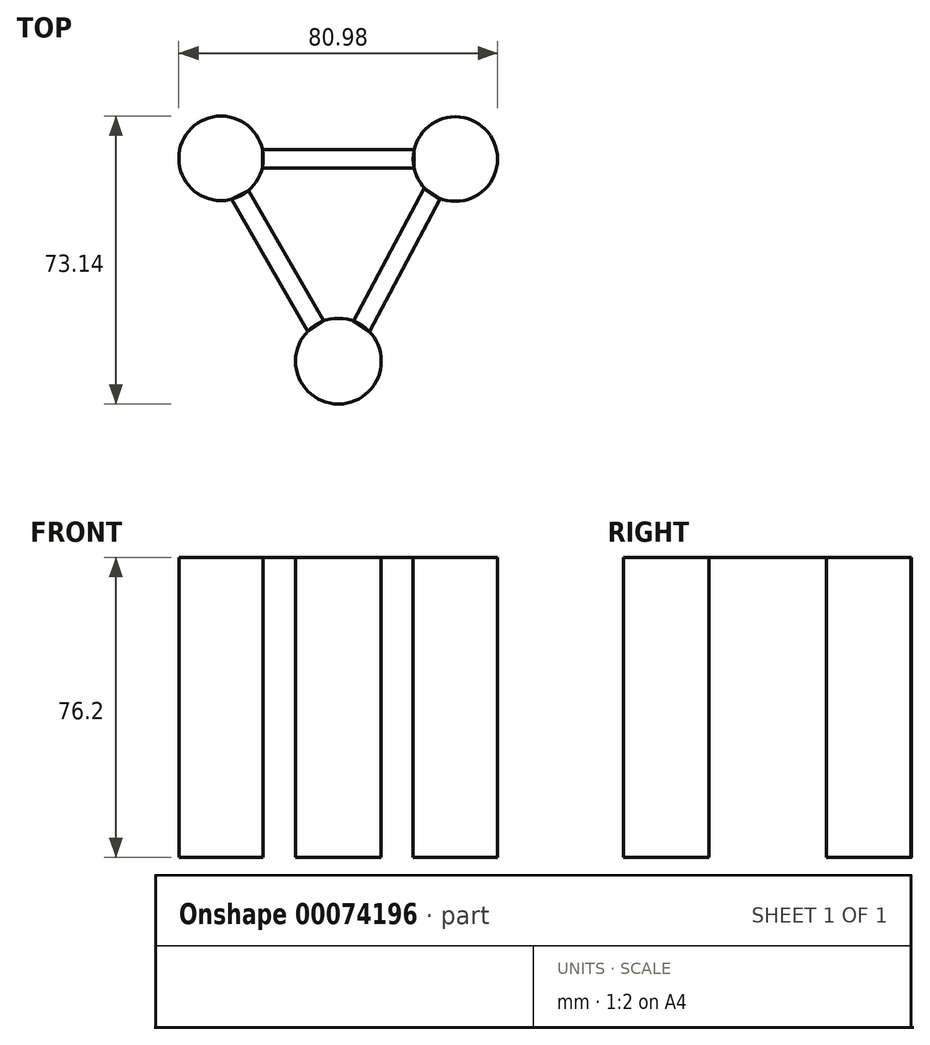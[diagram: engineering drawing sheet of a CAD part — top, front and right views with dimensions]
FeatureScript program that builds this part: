
annotation { "Feature Type Name" : "Feature", "Feature Type Description" : "" }
export const myFeature = defineFeature(function(context is Context, id is Id, definition is map)
    precondition{}
    {
        {
            var Q0;
            Q0=qCreatedBy(makeId("Top.planeOp"),FACE);
            var sketch = newSketch(context, id + "F0", { "sketchPlane" : qUnion([Q0])});
            skCircle(sketch, "E0", {"center": v(-29.82, 21.2) * mm, "radius": 10.73 * mm});
            skCircle(sketch, "E1", {"center": v(29.7, 21.02) * mm, "radius": 10.73 * mm});
            skCircle(sketch, "E2", {"center": v(0, -30.33) * mm, "radius": 10.89 * mm});
            skSolve(sketch);
        }
        {
            var Q0;
            Q0 = qSketchRegion(id + "F0", true);
            extrude(context, id + "F1", {"entities" : qUnion([Q0]), "oppositeDirection" : true, "depth" : 76.2 * mm});
        }
        {
            var Q0;
            Q0=qCreatedBy(makeId("Top.planeOp"),FACE);
            var sketch = newSketch(context, id + "F2", { "sketchPlane" : qUnion([Q0])});
            skLineSegment(sketch, "E3", {"start": v(-19.33, 18.77) * mm, "end": v(19.22, 18.77) * mm});
            skLineSegment(sketch, "E4", {"start": v(19.22, 23.45) * mm, "end": v(-19.28, 23.45) * mm});
            skLineSegment(sketch, "E5", {"start": v(-7.79, -22.7) * mm, "end": v(-27.1, 10.86) * mm});
            skLineSegment(sketch, "E6", {"start": v(-27.1, 10.86) * mm, "end": v(-22.85, 12.96) * mm});
            skLineSegment(sketch, "E7", {"start": v(-22.85, 12.96) * mm, "end": v(-3.77, -20.05) * mm});
            skLineSegment(sketch, "E8", {"start": v(-7.79, -22.7) * mm, "end": v(-3.77, -20.05) * mm});
            skLineSegment(sketch, "E9", {"start": v(-19.33, 18.77) * mm, "end": v(-19.28, 23.45) * mm});
            skLineSegment(sketch, "E10", {"start": v(19.22, 23.45) * mm, "end": v(19.22, 18.77) * mm});
            skLineSegment(sketch, "E11", {"start": v(3.8, -20.1) * mm, "end": v(21.74, 13.58) * mm});
            skLineSegment(sketch, "E12", {"start": v(7.92, -22.74) * mm, "end": v(25.84, 10.9) * mm});
            skLineSegment(sketch, "E13", {"start": v(3.8, -20.1) * mm, "end": v(7.92, -22.74) * mm});
            skLineSegment(sketch, "E14", {"start": v(21.74, 13.58) * mm, "end": v(25.84, 10.9) * mm});
            skSolve(sketch);
        }
        {
            var Q0;
            Q0 = qSketchRegion(id + "F2", true);
            extrude(context, id + "F3", {"entities" : qUnion([Q0]), "oppositeDirection" : true, "depth" : 1 / 50.8 * mm});
        }
    });
